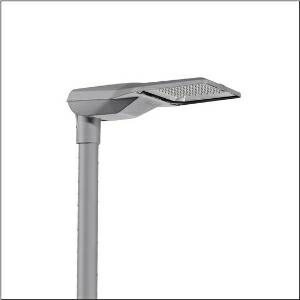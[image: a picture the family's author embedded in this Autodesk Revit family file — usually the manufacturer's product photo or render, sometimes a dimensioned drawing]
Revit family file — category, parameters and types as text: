
# Revit family: streetlight_sl_21_iq_midi___p0_8a_5xe3u31g08nb_121e
name_source: partatom
category: Lighting Fixtures
units: mm (PartAtom-declared; Revit-internal decimal feet)

## family parameters
Cut with Voids When Loaded = No
Host = Face
Light Source = No
Part Type = Normal
Room Calculation Point = No
Round Connector Dimension = Use Diameter
Shared = No

## types (1)
- --- (1 x LED, 23430 lm, 155.5 W, 3000K)
    Apparent Load = 155 VA
    CIE Flux Codes = 36 69 97 100 100
    Color Rendering = 70
    Color Temperature = 3000K
    Default Elevation = 1800 mm
    Description = Streetlight SL 21 iQ midi, mast luminaire, primary light control with lens, of PMMA, primary optical cover: cover, of toughened safety glass, transparent, light distribution: P0.8a, light emission: direct distribution, primary light characteristic: asymmetric, installation type: post-top, side-entry, LED, High Power LED, rated luminous flux: 23.430lm, luminous efficacy: 151lm/W, light colour: 730, colour temperature: 3000K, control gear: iQ Street-Remote, control: pre-setting: linear dimming characteristic, Street-Remote, Auto-Match, Temp-Guard, Lumen-Switch, Night-Set, Smart-Wire, Light-Fading, Desk-Remote (wireless, voltage-free reading and setting of iQ features in the workshop via application-optimized NFC function/RFID function), optimised constant luminous flux control (CLO 2.0), mains connection: 230..240V, AC, 50/60Hz, start of lifetime: 156W, end of service life: 162W, reduction: 69W, luminaire housing, of diecast aluminium, powder-coated, Siteco® metallic grey (DB 702S), corrosivity category C5 mid according to DIN EN ISO 12944, please order mast flange separately, inclination adjustable: 0°, 5°, 10°, 15°, sealing non-destructively replaceable, multi-level sealing system, length: 644mm, width: 335mm, height: 110mm, mast flange for spigot size: 42mm (side-entry): 5XC10008XM4, 60/48mm (side-entry/post-top): 5XC10108XM2, 76/60mm (side-entry/post-top): 5XC10108XM1, mounting height: 4..8m, protection rating (complete): IP66, insulation class (complete): insulation class II (safety insulation), certification: CE, ENEC, ENEC+, VDE, impact resistance: IK10, permissible operating ambient temperature for outdoor applications: -40..+50°C, standard-compliant lighting for roads and squares, packaging unit: 1 piece

Light Distribution: P0.8a
    Height = 111 mm
    Lamp = 1 x LED
    Lamp Light Flux = 23430 lm
    Lamp Power = 155.5 W
    Lamp count = 1
    Length = 644 mm
    Luminous efficacy = 151 lm/W
    Manufacturer = Siteco
    ModVariant = No
    Model = 5XE3U31G08NB
    Number of Poles = 1
    OnlyDefault = Yes
    Power Factor = 1
    Product Name = Streetlight SL 21 iQ midi | P0.8a
    Product group = mast luminaire | pylon top
    ProductGroupID = 6100
    Protection Class = Protection class II
    Protection Degree = IP 66
    RLX_Detail_Level = 1
    RLX_Emergency_Light_Flux = 0 lm
    RLX_Emergency_Type = 0
    RLX_Emergency_Type_DB = No
    RlxData = <blob elided: 26989 chars, md5=5474b067>
    Socket = socket
    Standby Power = 0 W
    System Light Flux = 23431 lm
    System Power = 155 W
    Type Comments = factory setting: luminous flux: 100 % | dim-lin: 254 | 823 mA
    Type Image = l_1004298.jpg
    URL = http://relux.com
    VarID = @adj_071516
    Voltage = 0 V
    Weight = 0.00 kg
    Width = 336 mm

## geometry (parser evidence)
native form markers: Blend x4, Sweep x13
no freeform markers — native parametric forms only
